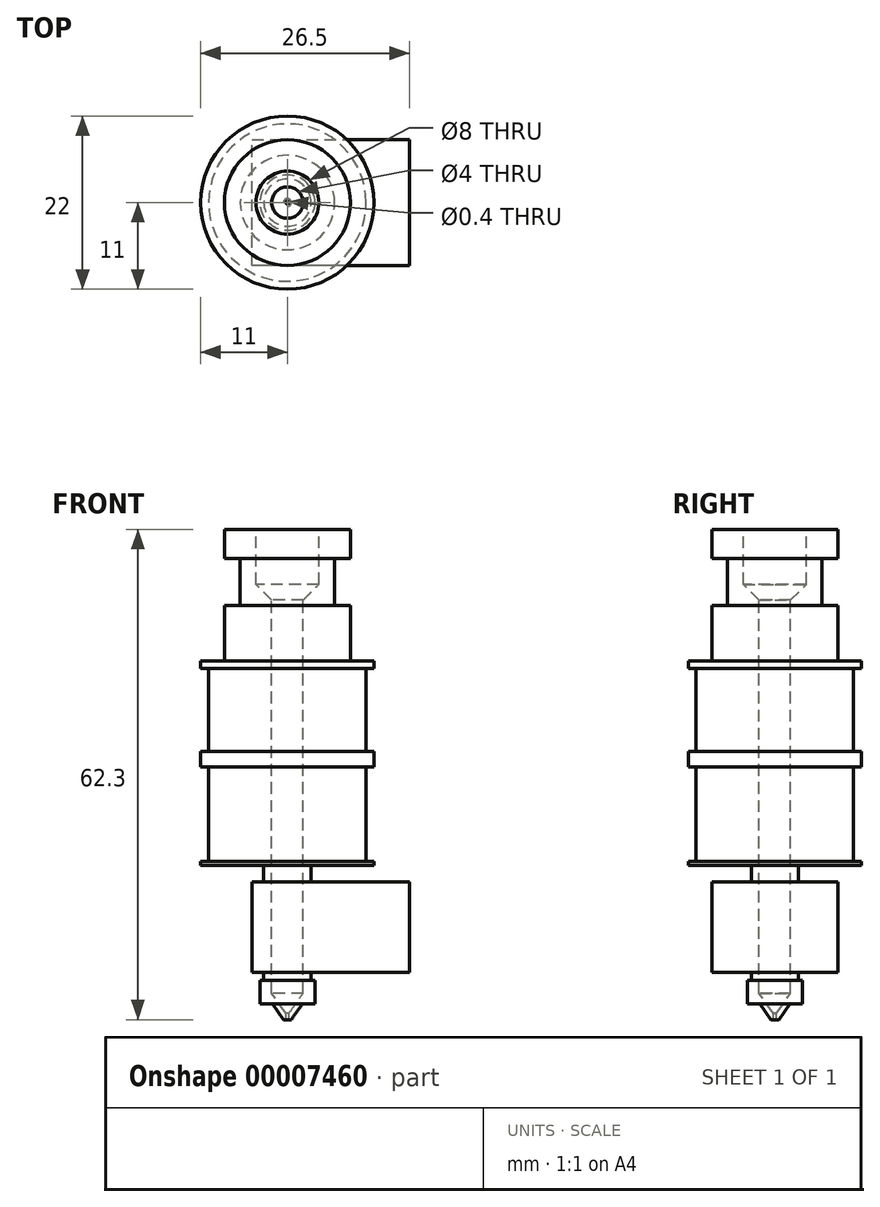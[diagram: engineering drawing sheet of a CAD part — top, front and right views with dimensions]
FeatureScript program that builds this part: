
annotation { "Feature Type Name" : "Feature", "Feature Type Description" : "" }
export const myFeature = defineFeature(function(context is Context, id is Id, definition is map)
    precondition{}
    {
        {
            var Q0;
            Q0=qCreatedBy(makeId("Front.planeOp"),FACE);
            var sketch = newSketch(context, id + "F0", { "sketchPlane" : qUnion([Q0])});
            skLineSegment(sketch, "E0", {"start": v(0, 0) * mm, "end": v(8, 0) * mm});
            skLineSegment(sketch, "E1", {"start": v(8, 0) * mm, "end": v(8, -3.7) * mm});
            skLineSegment(sketch, "E2", {"start": v(8, -3.7) * mm, "end": v(6, -3.7) * mm});
            skLineSegment(sketch, "E3", {"start": v(6, -3.7) * mm, "end": v(6, -9.7) * mm});
            skLineSegment(sketch, "E4", {"start": v(6, -9.7) * mm, "end": v(8, -9.7) * mm});
            skLineSegment(sketch, "E5", {"start": v(8, -9.7) * mm, "end": v(8, -16.7) * mm});
            skLineSegment(sketch, "E6", {"start": v(8, -16.7) * mm, "end": v(11, -16.7) * mm});
            skLineSegment(sketch, "E7", {"start": v(11, -16.7) * mm, "end": v(11, -17.7) * mm});
            skLineSegment(sketch, "E8", {"start": v(11, -17.7) * mm, "end": v(10, -17.7) * mm});
            skLineSegment(sketch, "E9", {"start": v(10, -17.7) * mm, "end": v(10, -28.2) * mm});
            skLineSegment(sketch, "E10", {"start": v(10, -28.2) * mm, "end": v(11, -28.2) * mm});
            skLineSegment(sketch, "E11", {"start": v(11, -28.2) * mm, "end": v(11, -30.2) * mm});
            skLineSegment(sketch, "E12", {"start": v(11, -30.2) * mm, "end": v(10, -30.2) * mm});
            skLineSegment(sketch, "E13", {"start": v(10, -30.2) * mm, "end": v(10, -42.2) * mm});
            skLineSegment(sketch, "E14", {"start": v(10, -42.2) * mm, "end": v(11, -42.2) * mm});
            skLineSegment(sketch, "E15", {"start": v(11, -42.2) * mm, "end": v(11, -42.7) * mm});
            skLineSegment(sketch, "E16", {"start": v(11, -42.7) * mm, "end": v(3, -42.7) * mm});
            skLineSegment(sketch, "E17", {"start": v(3, -57.3) * mm, "end": v(3.5, -57.3) * mm});
            skLineSegment(sketch, "E18", {"start": v(3.5, -57.3) * mm, "end": v(3.5, -60.3) * mm});
            skLineSegment(sketch, "E19", {"start": v(3.5, -60.3) * mm, "end": v(1.9, -60.3) * mm});
            skLineSegment(sketch, "E20", {"start": v(8, -9.7) * mm, "end": v(8, -3.7) * mm, "construction": true});
            skLineSegment(sketch, "E21", {"start": v(11, -17.7) * mm, "end": v(11, -28.2) * mm, "construction": true});
            skLineSegment(sketch, "E22", {"start": v(11, -30.2) * mm, "end": v(11, -42.2) * mm, "construction": true});
            skLineSegment(sketch, "E23", {"start": v(4, 0) * mm, "end": v(4, -7) * mm});
            skLineSegment(sketch, "E24", {"start": v(4, -7) * mm, "end": v(2, -9) * mm});
            skLineSegment(sketch, "E25", {"start": v(2, -9) * mm, "end": v(2, -58.93) * mm});
            skLineSegment(sketch, "E26", {"start": v(2, -58.93) * mm, "end": v(0.2, -61.5) * mm});
            skLineSegment(sketch, "E27", {"start": v(0.2, -61.5) * mm, "end": v(0.2, -62.3) * mm});
            skLineSegment(sketch, "E28", {"start": v(0.2, -62.3) * mm, "end": v(0.5, -62.3) * mm});
            skLineSegment(sketch, "E29", {"start": v(0.5, -62.3) * mm, "end": v(1.9, -60.3) * mm});
            skLineSegment(sketch, "E30", {"start": v(10, -28.2) * mm, "end": v(10, -30.2) * mm, "construction": true});
            skLineSegment(sketch, "E31", {"start": v(3, -42.7) * mm, "end": v(3, -49.8) * mm});
            skLineSegment(sketch, "E32", {"start": v(3, -49.8) * mm, "end": v(3, -57.3) * mm});
            skLineSegment(sketch, "E33", {"start": v(0, 0) * mm, "end": v(0, -84) * mm});
            skSolve(sketch);
        }
        {
            var Q0;
            {var subQ2=sQuery(id+"F0.wireOp",EDGE,"E1");Q0=makeQuery(id+"F0.imprint","IMPRINT",FACE,{"disambiguationData":[TD([[makeQuery(id+"F0.imprint","IMPRINT",EDGE,{"derivedFrom":subQ2}),-1.0]])]});}
            var Q1;
            Q1=sQuery(id+"F0.wireOp",EDGE,"E33");
            revolve(context, id + "F1", {"entities" : qUnion([Q0]), "axis" : qUnion([Q1]), "revolveType" : RevolveType.FULL});
        }
        {
            var Q0;
            Q0=qCreatedBy(makeId("Top.planeOp"),FACE);
            cPlane(context, id + "F2", {"entities" : qUnion([Q0]), "cplaneType" : CPlaneType.OFFSET, "offset" : 44.8 * mm, "oppositeDirection" : true, "width" : 150 * mm, "height" : 150 * mm});
        }
        {
            var Q0;
            Q0=qCreatedBy(id+"F2.planeOp",FACE);
            var sketch = newSketch(context, id + "F3", { "sketchPlane" : qUnion([Q0])});
            skCircle(sketch, "E34", {"center": v(0, 0) * mm, "radius": 3 * mm});
            skLineSegment(sketch, "E35", {"start": v(-4.5, 8) * mm, "end": v(15.5, 8) * mm});
            skLineSegment(sketch, "E36", {"start": v(15.5, 8) * mm, "end": v(15.5, -8) * mm});
            skLineSegment(sketch, "E37", {"start": v(15.5, -8) * mm, "end": v(-4.5, -8) * mm});
            skLineSegment(sketch, "E38", {"start": v(-4.5, -8) * mm, "end": v(-4.5, 8) * mm});
            skLineSegment(sketch, "E39", {"start": v(0, 0) * mm, "end": v(-4.5, 0) * mm, "construction": true});
            skSolve(sketch);
        }
        {
            var Q0;
            Q0=makeQuery(id+"F3.imprint","IMPRINT",FACE,{"disambiguationData":[TD([[makeQuery(id+"F3.imprint","IMPRINT",EDGE,{"derivedFrom":sQuery(id+"F3.wireOp",EDGE,"E34")}),-1.0]])]});
            extrude(context, id + "F4", {"entities" : qUnion([Q0]), "operationType" : NewBodyOperationType.ADD, "oppositeDirection" : true, "depth" : 11.5 * mm});
        }
    });
